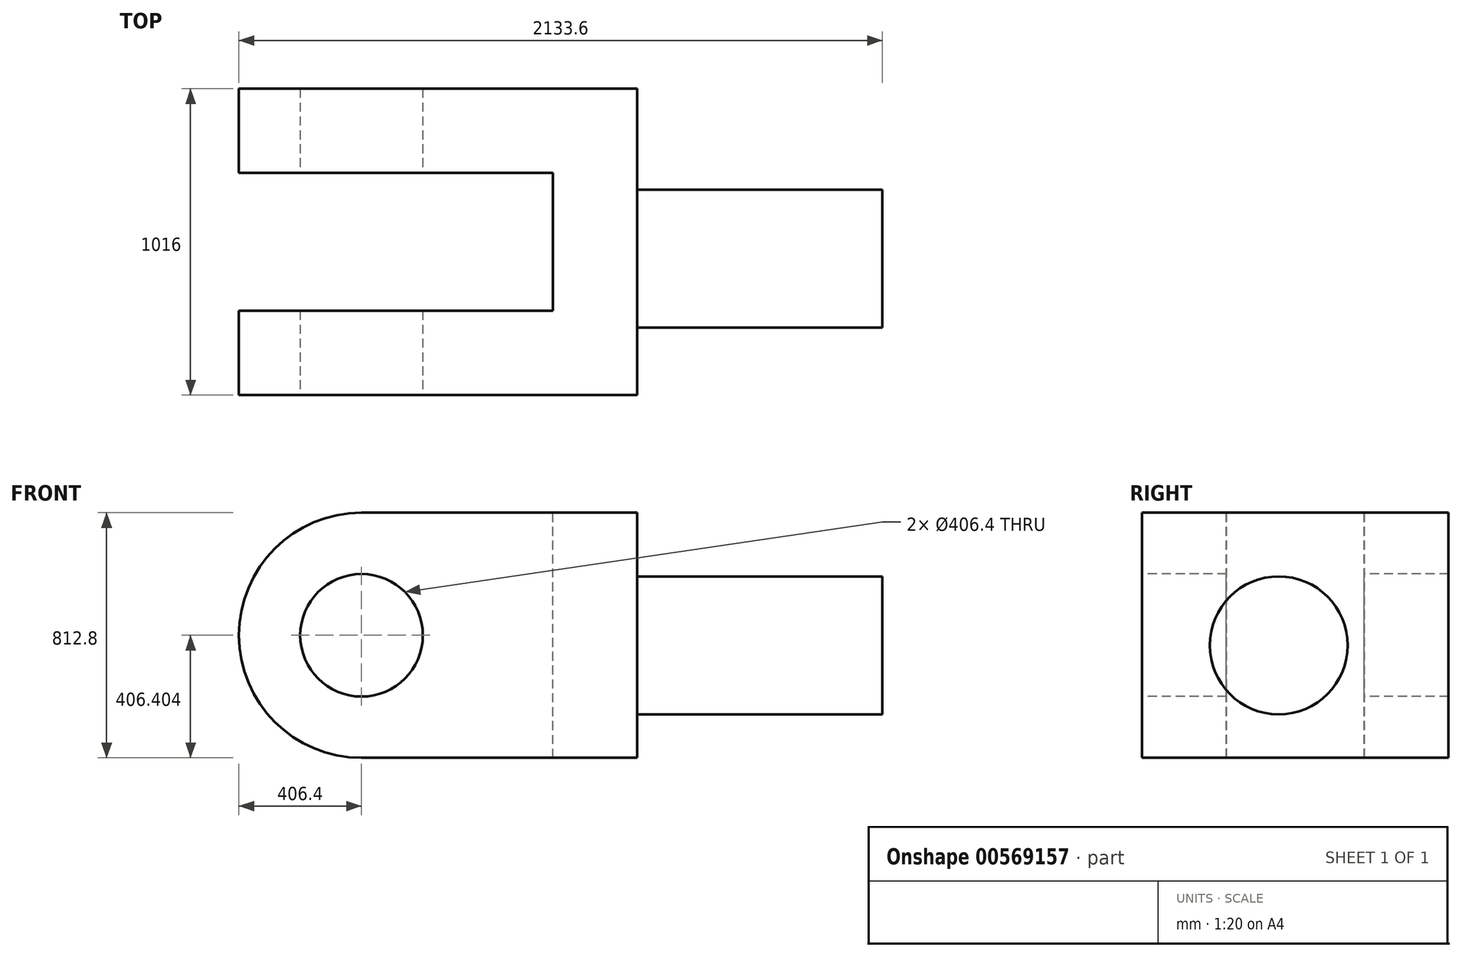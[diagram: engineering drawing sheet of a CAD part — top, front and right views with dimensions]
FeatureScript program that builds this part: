
annotation { "Feature Type Name" : "Feature", "Feature Type Description" : "" }
export const myFeature = defineFeature(function(context is Context, id is Id, definition is map)
    precondition{}
    {
        {
            var Q0;
            Q0=qCreatedBy(makeId("Right.planeOp"),FACE);
            var sketch = newSketch(context, id + "F0", { "sketchPlane" : qUnion([Q0])});
            skLineSegment(sketch, "E0", {"start": v(-123, -69.18) * mm, "end": v(893, -69.18) * mm});
            skLineSegment(sketch, "E1", {"start": v(893, -69.18) * mm, "end": v(893, 743.62) * mm});
            skLineSegment(sketch, "E2", {"start": v(893, 743.62) * mm, "end": v(-123, 743.62) * mm});
            skLineSegment(sketch, "E3", {"start": v(-123, 743.62) * mm, "end": v(-123, -69.18) * mm});
            skCircle(sketch, "E4", {"center": v(330.03, 303.78) * mm, "radius": 228.6 * mm});
            skSolve(sketch);
        }
        {
            var Q0;
            Q0=makeQuery(id+"F0.imprint","IMPRINT",FACE,{"disambiguationData":[TD([[makeQuery(id+"F0.imprint","IMPRINT",EDGE,{"derivedFrom":sQuery(id+"F0.wireOp",EDGE,"E4")}),1.0]])]});
            extrude(context, id + "F1", {"entities" : qUnion([Q0]), "depth" : 812.8 * mm, "offsetDistance" : 25.4 * mm});
        }
        {
            var Q0;
            Q0 = qSketchRegion(id + "F0", true);
            var Q1;
            Q1=makeQuery(id+"F1.opExtrude","CAP_FACE",FACE,{"disambiguationData":[OSD([sQuery(id+"F0.wireOp",EDGE,"E4")])],"isStart":true});
            extrude(context, id + "F2", {"entities" : qUnion([Q0, Q1]), "operationType" : NewBodyOperationType.ADD, "oppositeDirection" : true, "depth" : 914.4 * mm, "offsetDistance" : 25.4 * mm});
        }
        {
            var Q0;
            Q0=makeQuery(id+"F2.opExtrude","SWEPT_FACE",FACE,{"disambiguationData":[OSD([sQuery(id+"F0.wireOp",EDGE,"E3")])]});
            var sketch = newSketch(context, id + "F3", { "sketchPlane" : qUnion([Q0])});
            skLineSegment(sketch, "E5", {"start": v(-914.4, -69.18) * mm, "end": v(-914.4, 279.27) * mm});
            skLineSegment(sketch, "E6", {"start": v(-914.4, -69.18) * mm, "end": v(-914.4, 337.22) * mm});
            skCircle(sketch, "E7", {"center": v(-914.4, 337.22) * mm, "radius": 203.2 * mm});
            skArc(sketch, "E8", {"start": v(-914.4, 743.62) * mm, "mid": v(-1320.8, 337.22) * mm, "end": v(-914.4, -69.18) * mm});
            skLineSegment(sketch, "E9", {"start": v(-914.4, 743.62) * mm, "end": v(-914.4, 540.42) * mm});
            skSolve(sketch);
        }
        {
            var Q0;
            {var subQ0=sQuery(id+"F3.wireOp",EDGE,"E8");Q0=makeQuery(id+"F3.imprint","IMPRINT",FACE,{"disambiguationData":[TD([[makeQuery(id+"F3.imprint","IMPRINT",EDGE,{"derivedFrom":subQ0}),1.0]])]});}
            extrude(context, id + "F4", {"entities" : qUnion([Q0]), "operationType" : NewBodyOperationType.ADD, "oppositeDirection" : true, "depth" : 279.4 * mm, "offsetDistance" : 25.4 * mm});
        }
        {
            var Q0;
            Q0=makeQuery(id+"F4.boolean.opBoolean","MERGE",FACE,{"derivedFrom":[makeQuery(id+"F2.opExtrude","SWEPT_FACE",FACE,{"disambiguationData":[OSD([sQuery(id+"F0.wireOp",EDGE,"E3")])]}),makeQuery(id+"F4.opExtrude","CAP_FACE",FACE,{"disambiguationData":[OSD([sQuery(id+"F3.wireOp",EDGE,"E6"),sQuery(id+"F3.wireOp",EDGE,"E7"),sQuery(id+"F3.wireOp",EDGE,"E8"),sQuery(id+"F3.wireOp",EDGE,"E9")])],"isStart":true})]});
            var sketch = newSketch(context, id + "F5", { "sketchPlane" : qUnion([Q0])});
            skLineSegment(sketch, "E10", {"start": v(-914.4, 134.02) * mm, "end": v(-914.4, 540.42) * mm});
            skCircle(sketch, "E11", {"center": v(-914.4, 337.22) * mm, "radius": 203.2 * mm});
            skSolve(sketch);
        }
        {
            var Q0;
            {var subQ0=sQuery(id+"F5.wireOp",EDGE,"E10");Q0=makeQuery(id+"F5.imprint","IMPRINT",FACE,{"disambiguationData":[TD([[makeQuery(id+"F5.imprint","IMPRINT",EDGE,{"derivedFrom":subQ0}),1.0]])]});}
            extrude(context, id + "F6", {"entities" : qUnion([Q0]), "operationType" : NewBodyOperationType.REMOVE, "endBound" : BoundingType.THROUGH_ALL, "oppositeDirection" : true, "depth" : 25.4 * mm, "offsetDistance" : 25.4 * mm});
        }
        {
            var Q0;
            Q0=makeQuery(id+"F2.opExtrude","SWEPT_FACE",FACE,{"disambiguationData":[OSD([sQuery(id+"F0.wireOp",EDGE,"E2")])]});
            var sketch = newSketch(context, id + "F7", { "sketchPlane" : qUnion([Q0])});
            skLineSegment(sketch, "E12", {"start": v(0, 893) * mm, "end": v(-1320.8, 893) * mm});
            skLineSegment(sketch, "E13", {"start": v(-1320.8, 893) * mm, "end": v(-1320.8, 613.6) * mm});
            skLineSegment(sketch, "E14", {"start": v(-1320.8, 613.6) * mm, "end": v(-279.4, 613.6) * mm});
            skLineSegment(sketch, "E15", {"start": v(-279.4, 613.6) * mm, "end": v(-279.4, 156.4) * mm});
            skLineSegment(sketch, "E16", {"start": v(-279.4, 156.4) * mm, "end": v(-1320.8, 156.4) * mm});
            skLineSegment(sketch, "E17", {"start": v(-1320.8, 156.4) * mm, "end": v(-1320.8, -123) * mm});
            skLineSegment(sketch, "E18", {"start": v(-1320.8, -123) * mm, "end": v(0, -123) * mm});
            skSolve(sketch);
        }
        {
            var Q0;
            Q0 = qSketchRegion(id + "F7", true);
            var Q1;
            {var subQ0=sQuery(id+"F7.wireOp",EDGE,"E15");Q1=makeQuery(id+"F7.imprint","IMPRINT",FACE,{"disambiguationData":[TD([[makeQuery(id+"F7.imprint","IMPRINT",EDGE,{"derivedFrom":subQ0}),-1.0]])]});}
            extrude(context, id + "F8", {"entities" : qUnion([Q0, Q1]), "operationType" : NewBodyOperationType.REMOVE, "endBound" : BoundingType.THROUGH_ALL, "oppositeDirection" : true, "depth" : 25.4 * mm, "offsetDistance" : 25.4 * mm});
        }
        {
            var Q0;
            Q0=makeQuery(id+"F8.boolean.opBoolean","COPY",FACE,{"derivedFrom":makeQuery(id+"F8.opExtrude","SWEPT_FACE",FACE,{"disambiguationData":[OSD([sQuery(id+"F7.wireOp",EDGE,"E14")])]})});
            var sketch = newSketch(context, id + "F9", { "sketchPlane" : qUnion([Q0])});
            skArc(sketch, "E19", {"start": v(-914.4, 743.62) * mm, "mid": v(-1320.8, 337.22) * mm, "end": v(-914.4, -69.18) * mm});
            skLineSegment(sketch, "E20", {"start": v(-914.4, 743.62) * mm, "end": v(-914.4, 540.42) * mm});
            skLineSegment(sketch, "E21", {"start": v(-914.4, 134.02) * mm, "end": v(-914.4, -69.18) * mm});
            skArc(sketch, "E22", {"start": v(-914.4, 540.42) * mm, "mid": v(-1117.6, 337.22) * mm, "end": v(-914.4, 134.02) * mm});
            skSolve(sketch);
        }
        {
            var Q0;
            Q0=makeQuery(id+"F9.imprint","IMPRINT",FACE,{"disambiguationData":[TD([[makeQuery(id+"F9.imprint","IMPRINT",EDGE,{"derivedFrom":sQuery(id+"F9.wireOp",EDGE,"E19")}),1.0]])]});
            extrude(context, id + "F10", {"entities" : qUnion([Q0]), "operationType" : NewBodyOperationType.ADD, "oppositeDirection" : true, "depth" : 279.4 * mm, "offsetDistance" : 25.4 * mm});
        }
    });
